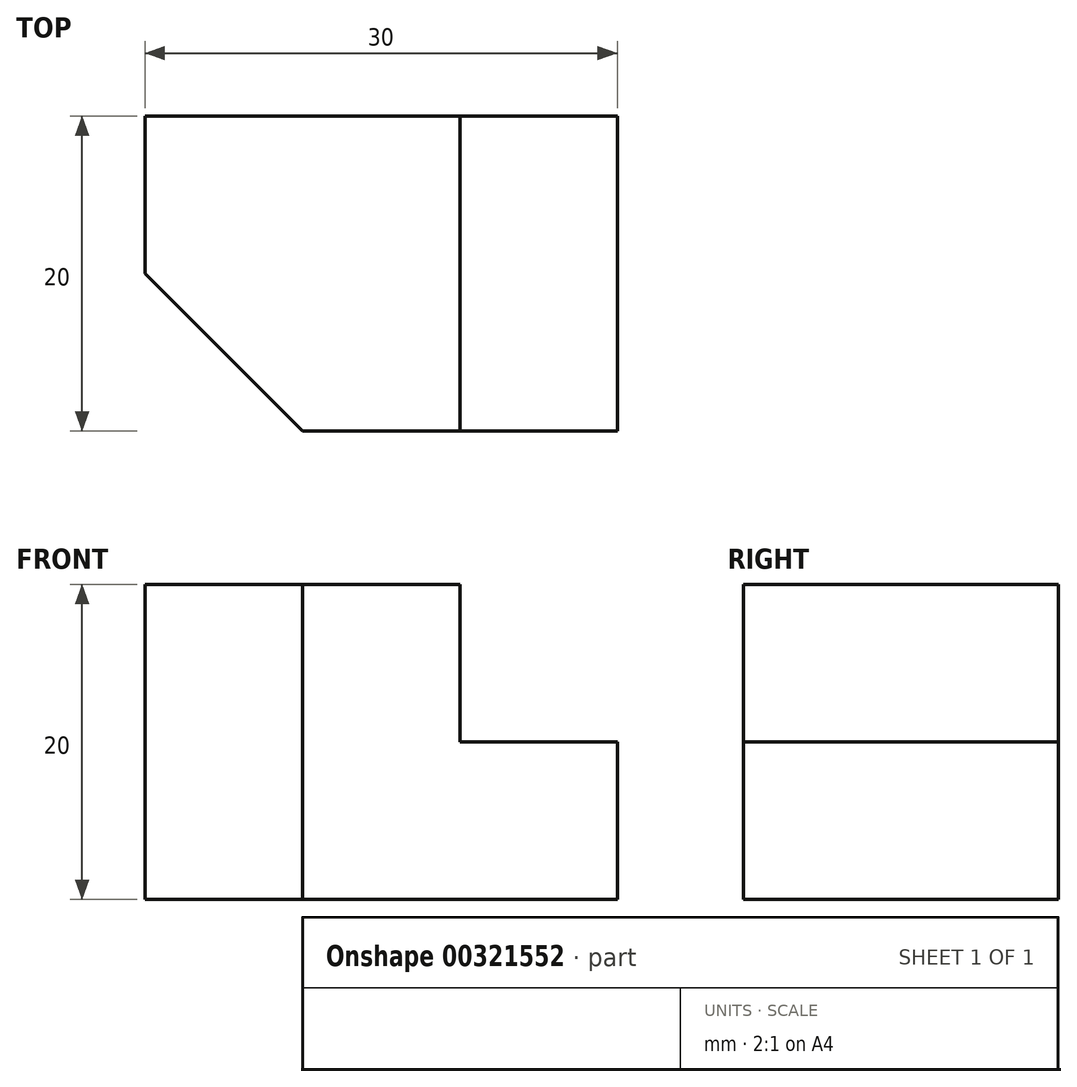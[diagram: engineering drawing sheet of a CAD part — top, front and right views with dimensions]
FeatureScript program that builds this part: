
annotation { "Feature Type Name" : "Feature", "Feature Type Description" : "" }
export const myFeature = defineFeature(function(context is Context, id is Id, definition is map)
    precondition{}
    {
        {
            var Q0;
            Q0=qCreatedBy(makeId("Top.planeOp"),FACE);
            var sketch = newSketch(context, id + "F0", { "sketchPlane" : qUnion([Q0])});
            skLineSegment(sketch, "E0.bottom", {"start": v(10, 0) * mm, "end": v(30, 0) * mm});
            skLineSegment(sketch, "E0.top", {"start": v(0, 20) * mm, "end": v(30, 20) * mm});
            skLineSegment(sketch, "E0.left", {"start": v(0, 10) * mm, "end": v(0, 20) * mm});
            skLineSegment(sketch, "E0.right", {"start": v(30, 0) * mm, "end": v(30, 20) * mm});
            skLineSegment(sketch, "E1", {"start": v(0, 10) * mm, "end": v(10, 0) * mm});
            skPoint(sketch, "E2.orphan", {"position": v(0, 0) * mm});
            skSolve(sketch);
        }
        {
            var Q0;
            Q0=makeQuery(id+"F0.imprint","IMPRINT",FACE,{"disambiguationData":[TD([[makeQuery(id+"F0.imprint","IMPRINT",EDGE,{"derivedFrom":sQuery(id+"F0.wireOp",EDGE,"E0.bottom")}),1.0]])]});
            extrude(context, id + "F1", {"entities" : qUnion([Q0]), "depth" : 10 * mm});
        }
        {
            var Q0;
            Q0=makeQuery(id+"F1.opExtrude","CAP_FACE",FACE,{"disambiguationData":[OSD([sQuery(id+"F0.wireOp",EDGE,"E0.bottom"),sQuery(id+"F0.wireOp",EDGE,"E0.top"),sQuery(id+"F0.wireOp",EDGE,"E0.left"),sQuery(id+"F0.wireOp",EDGE,"E0.right"),sQuery(id+"F0.wireOp",EDGE,"E1")])],"isStart":false});
            var sketch = newSketch(context, id + "F2", { "sketchPlane" : qUnion([Q0])});
            skLineSegment(sketch, "E3", {"start": v(20, 20) * mm, "end": v(20, 0) * mm});
            skSolve(sketch);
        }
        {
            var Q0;
            {var subQ2=sQuery(id+"F2.wireOp",EDGE,"E3");Q0=makeQuery(id+"F2.imprint","IMPRINT",FACE,{"disambiguationData":[TD([[makeQuery(id+"F2.imprint","IMPRINT",EDGE,{"derivedFrom":subQ2}),-1.0]])]});}
            extrude(context, id + "F3", {"entities" : qUnion([Q0]), "operationType" : NewBodyOperationType.ADD, "depth" : 10 * mm});
        }
    });
